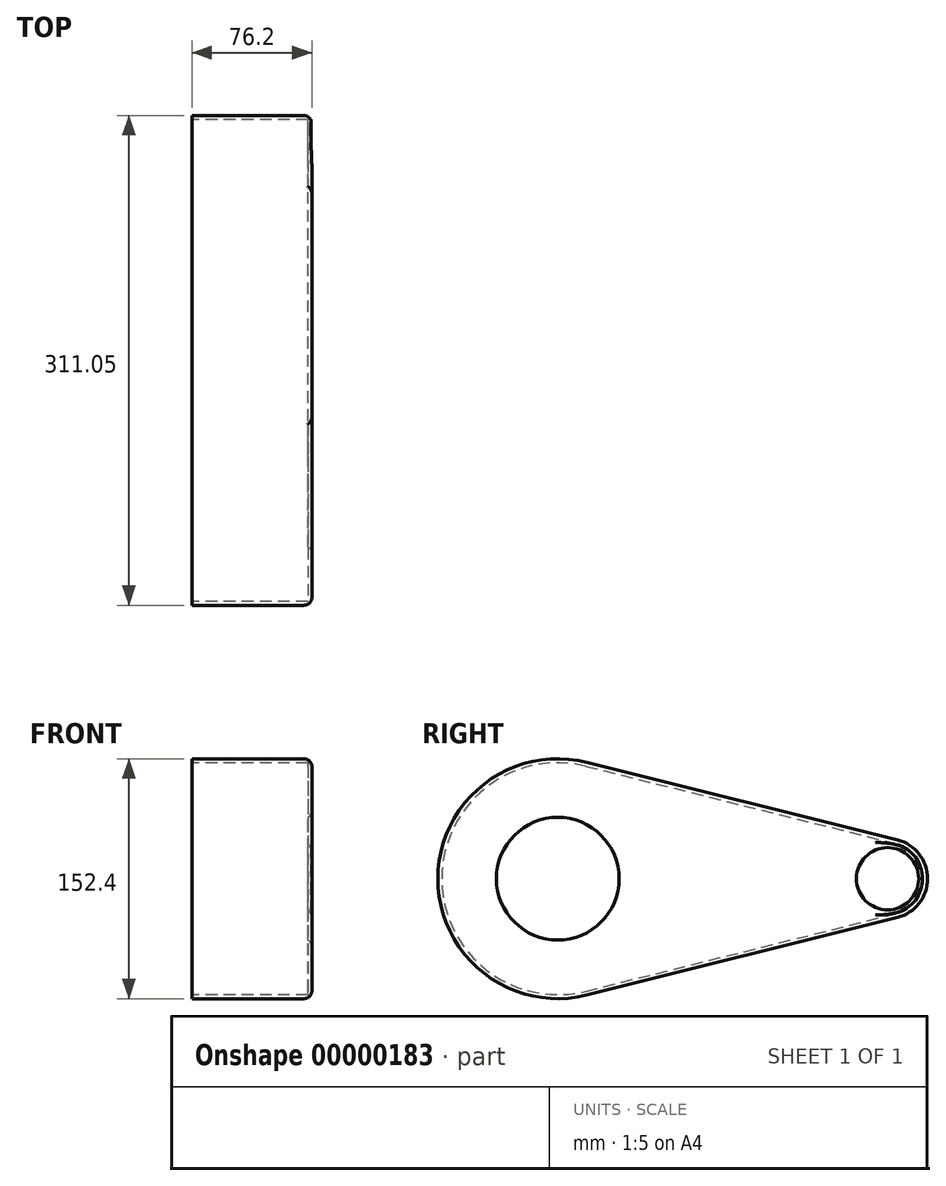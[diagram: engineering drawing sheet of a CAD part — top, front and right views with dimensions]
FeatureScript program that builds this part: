
annotation { "Feature Type Name" : "Feature", "Feature Type Description" : "" }
export const myFeature = defineFeature(function(context is Context, id is Id, definition is map)
    precondition{}
    {
        {
            var Q0;
            Q0=qCreatedBy(makeId("Right.planeOp"),FACE);
            var sketch = newSketch(context, id + "F0", { "sketchPlane" : qUnion([Q0])});
            skCircle(sketch, "E0", {"center": v(0, 0) * mm, "radius": 76.2 * mm});
            skCircle(sketch, "E1", {"center": v(209.45, 0) * mm, "radius": 25.4 * mm});
            skLineSegment(sketch, "E2", {"start": v(18.48, 73.92) * mm, "end": v(215.61, 24.64) * mm});
            skLineSegment(sketch, "E3", {"start": v(18.48, -73.92) * mm, "end": v(215.61, -24.64) * mm});
            skSolve(sketch);
        }
        {
            var Q0;
            {var subQ0=sQuery(id+"F0.wireOp",EDGE,"E1");var subQ2=makeQuery(id+"F0.imprint","INTERSECT",VERTEX,{"derivedFrom":[subQ0,sQuery(id+"F0.wireOp",EDGE,"E2")]});Q0=makeQuery(id+"F0.imprint","IMPRINT",FACE,{"disambiguationData":[TD([[makeQuery(id+"F0.imprint","IMPRINT",EDGE,{"disambiguationData":[TD([[subQ2,-1.0]])],"derivedFrom":subQ0}),1.0]])]});}
            var Q1;
            {var subQ1=sQuery(id+"F0.wireOp",EDGE,"E2");Q1=makeQuery(id+"F0.imprint","IMPRINT",FACE,{"disambiguationData":[TD([[makeQuery(id+"F0.imprint","IMPRINT",EDGE,{"derivedFrom":subQ1}),-1.0]])]});}
            var Q2;
            {var subQ0=sQuery(id+"F0.wireOp",EDGE,"E0");var subQ2=makeQuery(id+"F0.imprint","INTERSECT",VERTEX,{"derivedFrom":[subQ0,sQuery(id+"F0.wireOp",EDGE,"E2")]});Q2=makeQuery(id+"F0.imprint","IMPRINT",FACE,{"disambiguationData":[TD([[makeQuery(id+"F0.imprint","IMPRINT",EDGE,{"disambiguationData":[TD([[subQ2,-1.0]])],"derivedFrom":subQ0}),1.0]])]});}
            extrude(context, id + "F1", {"entities" : qUnion([Q0, Q1, Q2]), "depth" : 76.2 * mm});
        }
        {
            var Q0;
            Q0=makeQuery(id+"F1.opExtrude","CAP_FACE",FACE,{"disambiguationData":[OSD([sQuery(id+"F0.wireOp",EDGE,"E0"),sQuery(id+"F0.wireOp",EDGE,"E1"),sQuery(id+"F0.wireOp",EDGE,"E2"),sQuery(id+"F0.wireOp",EDGE,"E3")])],"isStart":false});
            var sketch = newSketch(context, id + "F2", { "sketchPlane" : qUnion([Q0])});
            skCircle(sketch, "E4", {"center": v(0, 0) * mm, "radius": 38.98 * mm});
            skCircle(sketch, "E5", {"center": v(209.45, 0) * mm, "radius": 19.78 * mm});
            skSolve(sketch);
        }
        {
            var Q0;
            Q0=makeQuery(id+"F1.opExtrude","CAP_FACE",FACE,{"disambiguationData":[OSD([sQuery(id+"F0.wireOp",EDGE,"E0"),sQuery(id+"F0.wireOp",EDGE,"E1"),sQuery(id+"F0.wireOp",EDGE,"E2"),sQuery(id+"F0.wireOp",EDGE,"E3")])],"isStart":true});
            shell(context, id + "F3", {"entities" : qUnion([Q0]), "thickness" : 2.54 * mm});
        }
        {
            var Q0;
            Q0=makeQuery(id+"F2.imprint","IMPRINT",FACE,{"disambiguationData":[TD([[makeQuery(id+"F2.imprint","IMPRINT",EDGE,{"derivedFrom":sQuery(id+"F2.wireOp",EDGE,"E4")}),1.0]])]});
            var Q1;
            Q1=makeQuery(id+"F2.imprint","IMPRINT",FACE,{"disambiguationData":[TD([[makeQuery(id+"F2.imprint","IMPRINT",EDGE,{"derivedFrom":sQuery(id+"F2.wireOp",EDGE,"E5")}),1.0]])]});
            extrude(context, id + "F4", {"entities" : qUnion([Q0, Q1]), "operationType" : NewBodyOperationType.REMOVE, "oppositeDirection" : true, "depth" : 50.8 * mm});
        }
        {
            var Q0;
            Q0=makeQuery(id+"F1.opExtrude","CAP_FACE",FACE,{"disambiguationData":[OSD([sQuery(id+"F0.wireOp",EDGE,"E0"),sQuery(id+"F0.wireOp",EDGE,"E1"),sQuery(id+"F0.wireOp",EDGE,"E2"),sQuery(id+"F0.wireOp",EDGE,"E3")])],"isStart":false});
            var Q1;
            Q1=makeQuery(id+"F4.opExtrude","CAP_EDGE",EDGE,{"disambiguationData":[OSD([sQuery(id+"F2.imprint",EDGE,"E5")])],"isStart":false});
            var Q2;
            Q2=makeQuery(id+"F4.opExtrude","CAP_EDGE",EDGE,{"disambiguationData":[OSD([sQuery(id+"F2.imprint",EDGE,"E4")])],"isStart":false});
            fillet(context, id + "F5", {"entities" : qUnion([Q0, Q1, Q2]), "radius" : 5.08 * mm, "tangentPropagation" : true, "allowEdgeOverflow" : false});
        }
    });
